# Revit family: 45771CHN_NEW
name_source: partatom
category: Furniture
revit_build: Autodesk Revit 2018 (Build: 20170223_1515(x64)
units: mm (PartAtom-declared; Revit-internal decimal feet)

## family parameters
Always vertical = No
Cut with Voids When Loaded = No
OmniClass Number = 23.40.20.00
OmniClass Title = General Furniture and Specialties
Room Calculation Point = No
Shared = No
Work Plane-Based = Yes

## types (1)
- 007 Chrome
    Always visible = Yes
    BIMobject category = Other Sanitary
    Default Elevation = 1219.2 mm  [stored 4 ft]
    Design country = Germany
    EAN code = 4059625130643
    Edition number = 1
    IFC Classification = Sanitary Terminal
    Installation instructions = https://www.axor-design.com
    Manufacturer country = Germany
    Manufacturer name = AXOR
    Material 1 = AXOR - AXOR One - 007 Chrome
    Material main = Chrome
    Product Guid = 570c819a-c7ae-48a0-a826-992ee590190b
    Product SKU = 45771CHN
    Product data url = https://www.bimobject.com
    Product family = AXOR One
    Product group = Shut-off valves
    Product name = 45771CHN AXOR One Shut-off valve for concealed installation
    Product url = https://www.axor-design.com
    QR code = https://www.bimobject.com
    Technical description = https://www.axor-design.com

note: [stored X ft] marks values corroborated as IEEE doubles in the binary element streams (Revit-internal decimal feet)

## geometry (parser evidence)
native form markers: Sweep x2
no freeform markers — native parametric forms only
